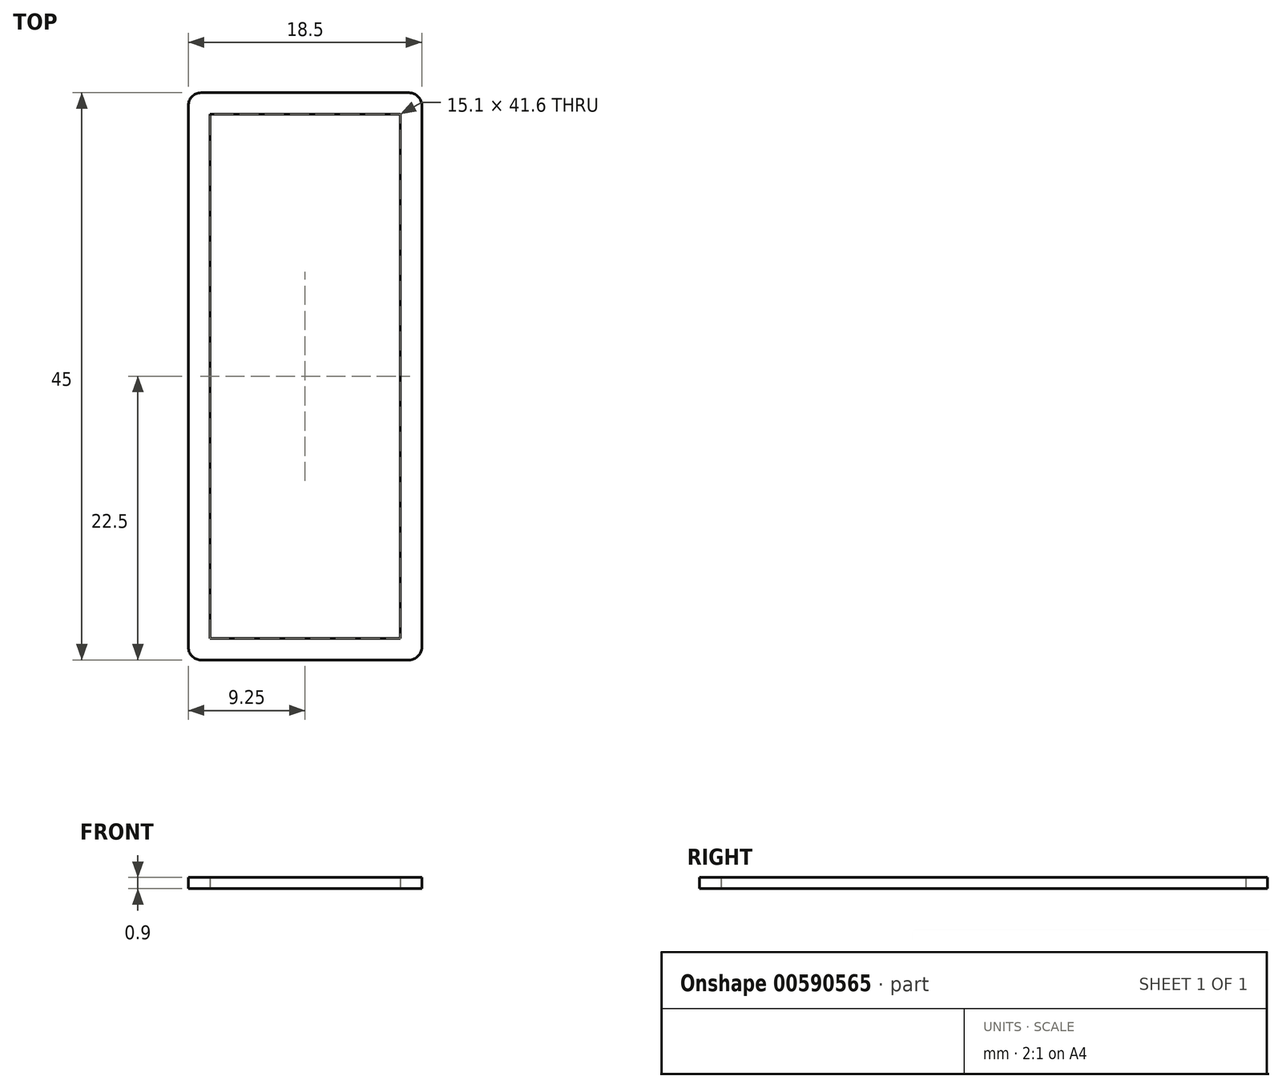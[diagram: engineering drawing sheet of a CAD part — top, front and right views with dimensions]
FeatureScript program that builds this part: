
annotation { "Feature Type Name" : "Feature", "Feature Type Description" : "" }
export const myFeature = defineFeature(function(context is Context, id is Id, definition is map)
    precondition{}
    {
        {
            var Q0;
            Q0=qCreatedBy(makeId("Top.planeOp"),FACE);
            var sketch = newSketch(context, id + "F0", { "sketchPlane" : qUnion([Q0])});
            skLineSegment(sketch, "E0.bottom", {"start": v(1, 0) * mm, "end": v(17.5, 0) * mm});
            skLineSegment(sketch, "E0.top", {"start": v(1, 45) * mm, "end": v(17.5, 45) * mm});
            skLineSegment(sketch, "E0.left", {"start": v(0, 1) * mm, "end": v(0, 44) * mm});
            skLineSegment(sketch, "E0.right", {"start": v(18.5, 1) * mm, "end": v(18.5, 44) * mm});
            skLineSegment(sketch, "E1.0", {"start": v(1.7, 43.3) * mm, "end": v(16.8, 43.3) * mm});
            skLineSegment(sketch, "E1.1", {"start": v(1.7, 1.7) * mm, "end": v(1.7, 43.3) * mm});
            skLineSegment(sketch, "E1.2", {"start": v(1.7, 1.7) * mm, "end": v(16.8, 1.7) * mm});
            skLineSegment(sketch, "E1.3", {"start": v(16.8, 1.7) * mm, "end": v(16.8, 43.3) * mm});
            skPoint(sketch, "E2.visualSharp", {"position": v(18.5, 0) * mm});
            skArc(sketch, "E2.filletArc", {"start": v(17.5, 0) * mm, "mid": v(18.2, 0.3) * mm, "end": v(18.5, 1) * mm});
            skPoint(sketch, "E3.visualSharp", {"position": v(0, 0) * mm});
            skArc(sketch, "E3.filletArc", {"start": v(0, 1) * mm, "mid": v(0.3, 0.3) * mm, "end": v(1, 0) * mm});
            skPoint(sketch, "E4.visualSharp", {"position": v(18.5, 45) * mm});
            skArc(sketch, "E4.filletArc", {"start": v(18.5, 44) * mm, "mid": v(18.2, 44.7) * mm, "end": v(17.5, 45) * mm});
            skPoint(sketch, "E5.visualSharp", {"position": v(0, 45) * mm});
            skArc(sketch, "E5.filletArc", {"start": v(1, 45) * mm, "mid": v(0.3, 44.7) * mm, "end": v(0, 44) * mm});
            skSolve(sketch);
        }
        {
            var Q0;
            Q0 = qSketchRegion(id + "F0", true);
            extrude(context, id + "F1", {"entities" : qUnion([Q0]), "depth" : .9 * mm, "offsetDistance" : 25 * mm});
        }
    });
